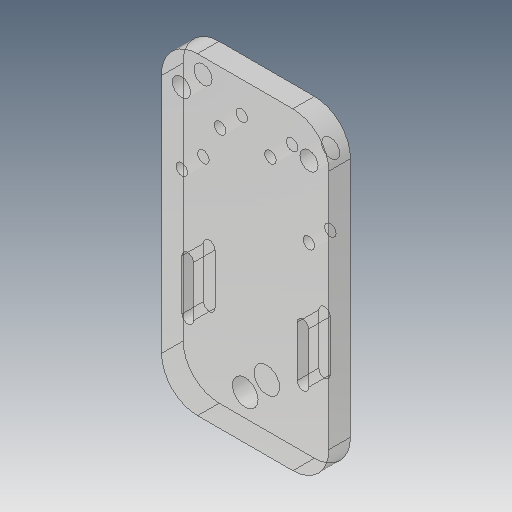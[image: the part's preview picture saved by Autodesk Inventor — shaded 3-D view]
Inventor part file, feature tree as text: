
AUTODESK INVENTOR PART (.ipt)
format: ipt  version: 2017 (Build 210142000, 142)  size: 209,920 bytes
history: native  units: in
note: dims shown in document units (in); Inventor stores cm internally (conversion verified against a paired STEP export)
features: reference x10, other x5, sketch x2, extrude x1
ambient origin geometry x8: Origin, YZ Plane, XZ Plane, XY Plane, X Axis, Y Axis, Z Axis, Center Point
bodies: Solid1 (feature_tree)
feature tree (18):
  sketch  "Sketch1"  dims[d7=0.2362in d8=0.0in]
  extrude  "Extrusion1"  [1 undecoded]
  reference  "Reference1"
  reference  "Reference2"
  reference  "Reference3"
  reference  "Reference4"
  sketch  "Sketch2"
  reference  "Reference5"
  reference  "Reference6"
  reference  "Reference7"
  reference  "Reference8"
  reference  "Reference9"
  reference  "Reference10"
  other  "<userpath>\OneDrive\Inventor\Beast 3D Printer\Hotend Mount Assembly.iam"
  other  "Hotend Mount Assembly.iam"
  other  "Hotend Front Plate:1"
  other  "Hotend Slide Part3:1"
  other  "Hotend Slide Part 1:1"
note: 1 required parameter value undecoded (feature->parameter linkage not recoverable at this tier; creation-order binding heuristic only, values carry confidence <= 0.55)
